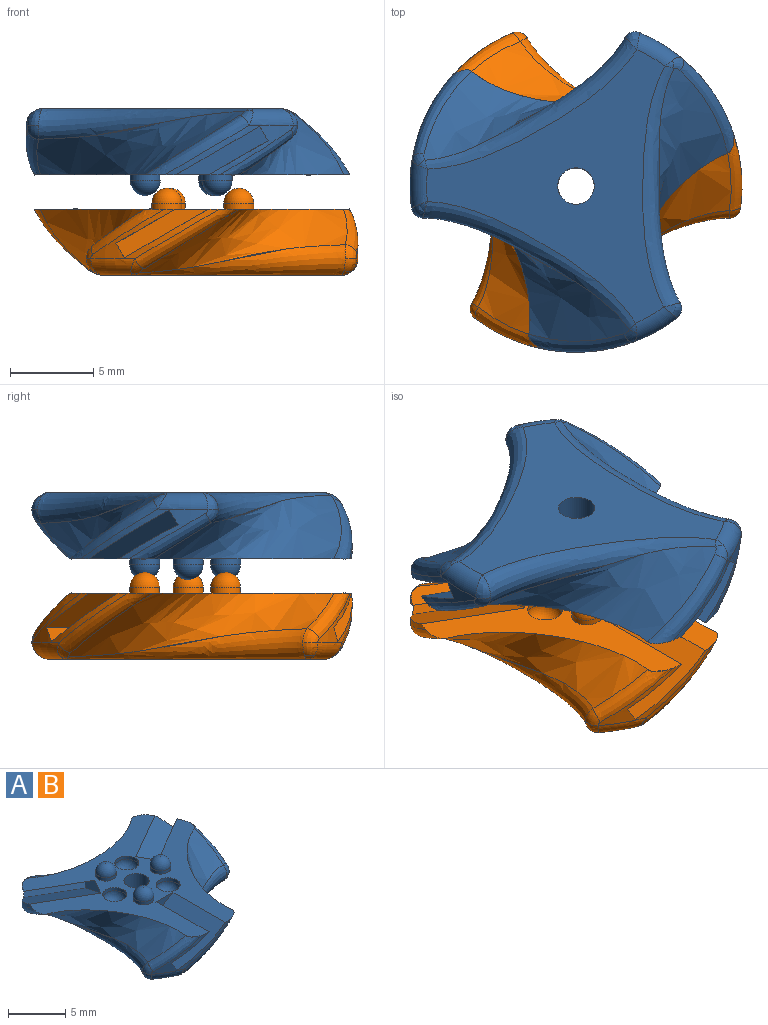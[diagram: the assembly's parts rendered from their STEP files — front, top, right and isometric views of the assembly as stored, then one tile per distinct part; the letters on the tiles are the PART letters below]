
ASSEMBLY  parts=2 mates=1
PART A: 60 faces, bbox 26.2x26.7x7.7 mm
  f0: plane 16.48x14.36mm, normal (0,0,-1), area 96.9mm2, adj f4,f43,f47,f49,f53,f55,f59
  f1: cylinder r=10mm len=7.67mm, axis (0,0,-1), area 4.8mm2, adj f3,f10,f11,f12,f36,f41,f42,f47
  f2: cylinder r=10mm len=5.74mm, axis (0,0,-1), area 4.8mm2, adj f3,f6,f7,f8,f37,f38,f54,f59
  f3: plane 19.37x17.33mm, normal (0,0,1), area 110.8mm2, adj f1,f2,f4,f5,f7,f8,f9,f11
  f4: cylinder r=1.1mm len=4mm, axis (0,0,-1), area 27.6mm2, adj f0,f3
  f5: cylinder r=10mm len=7.74mm, axis (0,0,-1), area 4.8mm2, adj f3,f14,f15,f16,f39,f40,f49,f51
  f6: plane 5.13x3.13mm, normal (-0.43,-0.75,0.5), area 5.5mm2, adj f2,f7,f8,f9
  f7: plane 7.43x5.85mm, normal (-0.25,-0.43,-0.87), area 25mm2, adj f2,f3,f6,f9
  f8: plane 8.19x7.28mm, normal (0.25,0.43,0.87), area 36.8mm2, adj f2,f3,f6,f9
  f9: plane 4.83x2.93mm, normal (-0.87,0.5,0), area 5mm2, adj f3,f6,f7,f8
  f10: plane 4.92x3.25mm, normal (-0.43,0.75,0.5), area 5.5mm2, adj f1,f11,f12,f13
  f11: plane 6.52x6.38mm, normal (-0.25,0.43,-0.87), area 25mm2, adj f1,f3,f10,f13
  f12: plane 7.69x7.48mm, normal (0.25,-0.43,0.87), area 36.8mm2, adj f1,f3,f10,f13
  f13: plane 4.83x2.93mm, normal (0.87,0.5,0), area 5mm2, adj f3,f10,f11,f12
  f14: plane 5.64x0.87mm, normal (0.87,0,0.5), area 5.5mm2, adj f5,f15,f16,f17
  f15: plane 6.51x3.64mm, normal (0.5,0,-0.87), area 25mm2, adj f3,f5,f14,f17
  f16: plane 6.57x5.15mm, normal (-0.5,0,0.87), area 36.8mm2, adj f3,f5,f14,f17
  f17: plane 5.58x2.93mm, normal (0,-1,0), area 5mm2, adj f3,f14,f15,f16
  f18: cylinder r=0.9mm len=1.8mm, axis (0,0,1), area 2mm2, adj f3,f19
  f19: sphere r=0.9mm, area 5.1mm2, adj f18
  f20: cylinder r=0.9mm len=1.8mm, axis (0,0,1), area 2mm2, adj f3,f21
  f21: sphere r=0.9mm, area 5.1mm2, adj f20
  f22: cylinder r=0.9mm len=1.8mm, axis (0,0,1), area 2mm2, adj f3,f23
  f23: sphere r=0.9mm, area 5.1mm2, adj f22
  f24: cylinder r=1.05mm len=2.1mm, axis (0,0,1), area 2.3mm2, adj f3,f26
  f25: plane 0.3x0.3mm, normal (0,0,1), area 0.1mm2, adj f26
  f26: torus R=0.15mm, axis (0,0,1), area 6.4mm2, adj f24,f25
  f27: cylinder r=1.05mm len=2.1mm, axis (0,0,1), area 2.3mm2, adj f3,f29
  f28: plane 0.3x0.3mm, normal (0,0,1), area 0.1mm2, adj f29
  f29: torus R=0.15mm, axis (0,0,1), area 6.4mm2, adj f27,f28
  f30: cylinder r=1.05mm len=2.1mm, axis (0,0,1), area 2.3mm2, adj f3,f32
  f31: plane 0.3x0.3mm, normal (0,0,1), area 0.1mm2, adj f32
  f32: torus R=0.15mm, axis (0,0,1), area 6.4mm2, adj f30,f31
  f33: bspline ~21.18x20.11mm, area 53.7mm2, adj f3,f40,f41,f43,f45
  f34: bspline ~23.86x16.66mm, area 53.7mm2, adj f3,f38,f39,f55,f57
  f35: bspline ~21.18x20.11mm, area 53.7mm2, adj f3,f36,f37,f48,f53
  f36: bspline ~6.68x4.94mm, area 6.8mm2, adj f1,f3,f35,f48
  f37: bspline ~5.1x3.94mm, area 5.1mm2, adj f2,f3,f35,f54
  f38: bspline ~6.79x4.94mm, area 6.8mm2, adj f2,f3,f34,f57
  f39: bspline ~5.54x3.94mm, area 5.1mm2, adj f3,f5,f34,f51
  f40: bspline ~7.7x4.94mm, area 6.8mm2, adj f3,f5,f33,f45
  f41: bspline ~5.99x3.94mm, area 5.1mm2, adj f1,f3,f33,f42
  f42: bspline ~1.01x0.82mm, area 0.8mm2, adj f1,f41,f43,f44
  f43: bspline ~13.93x8.28mm, area 22.9mm2, adj f0,f33,f42,f44,f46
  f44: bspline ~1.28x0.99mm, area 1mm2, adj f42,f43,f47
  f45: bspline ~1.28x1.14mm, area 0.6mm2, adj f33,f40,f46,f49
  f46: bspline ~0.75x0.63mm, area 0.1mm2, adj f43,f45,f49
  f47: torus R=9mm, axis (0,0,1), area 3.9mm2, adj f0,f1,f44,f48,f50
  f48: bspline ~1.28x1.16mm, area 0.6mm2, adj f35,f36,f47,f50
  f49: torus R=9mm, axis (0,0,1), area 3.9mm2, adj f0,f5,f45,f46,f52
  f50: bspline ~0.73x0.7mm, area 0.1mm2, adj f47,f48,f53
  f51: bspline ~1.03x1.01mm, area 0.8mm2, adj f5,f39,f52,f55
  f52: bspline ~1.3x1.07mm, area 0.7mm2, adj f49,f51,f55
  f53: bspline ~13.92x9.56mm, area 22.9mm2, adj f0,f35,f50,f54,f56
  f54: bspline ~1.07x1.01mm, area 0.8mm2, adj f2,f37,f53,f56
  f55: bspline ~16.12x4.75mm, area 22.9mm2, adj f0,f34,f51,f52,f58
  f56: bspline ~1.28x1.26mm, area 1mm2, adj f53,f54,f59
  f57: bspline ~1.28x1.28mm, area 0.6mm2, adj f34,f38,f58,f59
  f58: bspline ~0.77x0.66mm, area 0.1mm2, adj f55,f57,f59
  f59: torus R=9mm, axis (0,0,1), area 3.9mm2, adj f0,f2,f56,f57,f58
PART B: same geometry as A
PLACE A rot(axis=(0.87,-0.5,0),180deg) t=(0,0,21.63)mm
PLACE B t=(0,0,11.58)mm
MATE parallel B.f13 <-> A.f17  axis (0.87,0.5,0) through (3.03,1.75,15.58)mm
